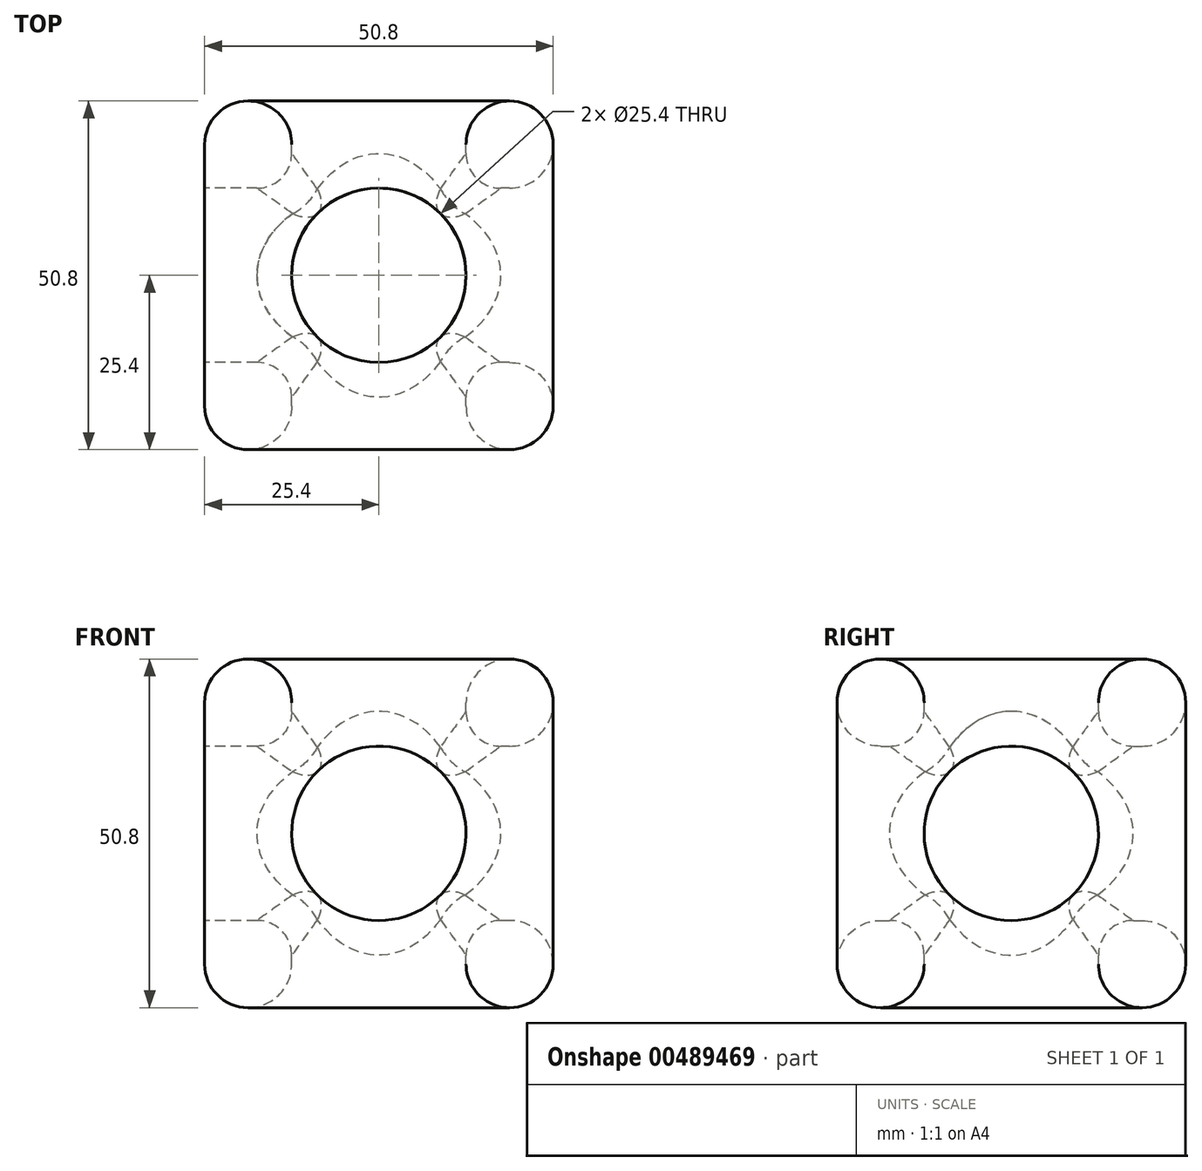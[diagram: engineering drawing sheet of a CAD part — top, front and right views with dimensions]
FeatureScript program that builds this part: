
annotation { "Feature Type Name" : "Feature", "Feature Type Description" : "" }
export const myFeature = defineFeature(function(context is Context, id is Id, definition is map)
    precondition{}
    {
        {
            var Q0;
            Q0=qCreatedBy(makeId("Front.planeOp"),FACE);
            var sketch = newSketch(context, id + "F0", { "sketchPlane" : qUnion([Q0])});
            skLineSegment(sketch, "E0", {"start": v(0, 0) * mm, "end": v(0, 50.8) * mm});
            skLineSegment(sketch, "E1", {"start": v(0, 50.8) * mm, "end": v(50.8, 50.8) * mm});
            skLineSegment(sketch, "E2", {"start": v(50.8, 50.8) * mm, "end": v(50.8, 0) * mm});
            skLineSegment(sketch, "E3", {"start": v(50.8, 0) * mm, "end": v(0, 0) * mm});
            skCircle(sketch, "E4", {"center": v(25.4, 25.4) * mm, "radius": 12.7 * mm});
            skSolve(sketch);
        }
        {
            var Q0;
            Q0 = qSketchRegion(id + "F0", true);
            extrude(context, id + "F1", {"entities" : qUnion([Q0]), "depth" : 50.8 * mm});
        }
        {
            var Q0;
            Q0=makeQuery(id+"F1.opExtrude","SWEPT_FACE",FACE,{"disambiguationData":[OSD([sQuery(id+"F0.wireOp",EDGE,"E0")])]});
            var sketch = newSketch(context, id + "F2", { "sketchPlane" : qUnion([Q0])});
            skPoint(sketch, "E5.trimOffspring.end.orphan", {"position": v(50.8, 50.8) * mm});
            skPoint(sketch, "E6.start.orphan", {"position": v(0, 50.8) * mm});
            skLineSegment(sketch, "E7", {"start": v(50.8, 0) * mm, "end": v(0, 0) * mm});
            skPoint(sketch, "E8.center.orphan", {"position": v(25.4, 50.8) * mm});
            skCircle(sketch, "E9", {"center": v(25.4, 25.4) * mm, "radius": 12.7 * mm});
            skSolve(sketch);
        }
        {
            var Q0;
            Q0 = qSketchRegion(id + "F2", true);
            extrude(context, id + "F3", {"entities" : qUnion([Q0]), "operationType" : NewBodyOperationType.REMOVE, "oppositeDirection" : true, "depth" : 50.8 * mm});
        }
        {
            var Q0;
            Q0 = qSketchRegion(id + "F2", true);
            extrude(context, id + "F4", {"entities" : qUnion([Q0]), "operationType" : NewBodyOperationType.REMOVE, "oppositeDirection" : true, "depth" : 50.8 * mm});
        }
        {
            var Q0;
            Q0=makeQuery(id+"F1.opExtrude","SWEPT_FACE",FACE,{"disambiguationData":[OSD([sQuery(id+"F0.wireOp",EDGE,"E1")])]});
            var sketch = newSketch(context, id + "F5", { "sketchPlane" : qUnion([Q0])});
            skCircle(sketch, "E10", {"center": v(25.4, -25.4) * mm, "radius": 12.7 * mm});
            skPoint(sketch, "E11.orphan", {"position": v(25.4, 0) * mm});
            skPoint(sketch, "E12.end.orphan", {"position": v(25.4, -50.8) * mm});
            skSolve(sketch);
        }
        {
            var Q0;
            Q0 = qSketchRegion(id + "F5", true);
            extrude(context, id + "F6", {"entities" : qUnion([Q0]), "operationType" : NewBodyOperationType.REMOVE, "oppositeDirection" : true, "depth" : 50.8 * mm});
        }
        {
            var Q0;
            Q0=makeQuery(id+"F1.opExtrude","SWEPT_EDGE",EDGE,{"disambiguationData":[OSD([sQuery(id+"F0.wireOp",EDGE,"E0"),sQuery(id+"F0.wireOp",EDGE,"E3")])]});
            var Q1;
            Q1=makeQuery(id+"F1.opExtrude","CAP_EDGE",EDGE,{"disambiguationData":[OSD([sQuery(id+"F0.wireOp",EDGE,"E0")])],"isStart":true});
            var Q2;
            Q2=makeQuery(id+"F1.opExtrude","SWEPT_FACE",FACE,{"disambiguationData":[OSD([sQuery(id+"F0.wireOp",EDGE,"E2")])]});
            var Q3;
            Q3=makeQuery(id+"F1.opExtrude","SWEPT_EDGE",EDGE,{"disambiguationData":[OSD([sQuery(id+"F0.wireOp",EDGE,"E2"),sQuery(id+"F0.wireOp",EDGE,"E3")])]});
            var Q4;
            Q4=makeQuery(id+"F1.opExtrude","CAP_EDGE",EDGE,{"disambiguationData":[OSD([sQuery(id+"F0.wireOp",EDGE,"E3")])],"isStart":true});
            var Q5;
            Q5=makeQuery(id+"F1.opExtrude","CAP_EDGE",EDGE,{"disambiguationData":[OSD([sQuery(id+"F0.wireOp",EDGE,"E3")])],"isStart":false});
            var Q6;
            Q6=makeQuery(id+"F6.boolean.opBoolean","COPY",EDGE,{"derivedFrom":makeQuery(id+"F6.opExtrude","CAP_EDGE",EDGE,{"disambiguationData":[OSD([sQuery(id+"F5.wireOp",EDGE,"E10")])],"isStart":false})});
            var Q7;
            Q7=makeQuery(id+"F1.opExtrude","SWEPT_FACE",FACE,{"disambiguationData":[OSD([sQuery(id+"F0.wireOp",EDGE,"E3")])]});
            var Q8;
            Q8=makeQuery(id+"F1.opExtrude","SWEPT_FACE",FACE,{"disambiguationData":[OSD([sQuery(id+"F0.wireOp",EDGE,"E1")])]});
            var Q9;
            Q9=makeQuery(id+"F3.boolean.opBoolean","COPY",EDGE,{"derivedFrom":makeQuery(id+"F3.opExtrude","CAP_EDGE",EDGE,{"disambiguationData":[OSD([sQuery(id+"F2.wireOp",EDGE,"E9")])],"isStart":true})});
            var Q10;
            Q10=makeQuery(id+"F1.opExtrude","CAP_EDGE",EDGE,{"disambiguationData":[OSD([sQuery(id+"F0.wireOp",EDGE,"E0")])],"isStart":false});
            var Q11;
            Q11=makeQuery(id+"F1.opExtrude","CAP_EDGE",EDGE,{"disambiguationData":[OSD([sQuery(id+"F0.wireOp",EDGE,"E4")])],"isStart":true});
            var Q12;
            Q12=makeQuery(id+"F1.opExtrude","CAP_EDGE",EDGE,{"disambiguationData":[OSD([sQuery(id+"F0.wireOp",EDGE,"E4")])],"isStart":false});
            fillet(context, id + "F7", {"entities" : qUnion([Q0, Q1, Q2, Q3, Q4, Q5, Q6, Q7, Q8, Q9, Q10, Q11, Q12]), "radius" : 6.35 * mm, "tangentPropagation" : true, "allowEdgeOverflow" : false});
        }
        {
            var Q0;
            {var subQ0=makeQuery(id+"F3.opExtrude","SWEPT_FACE",FACE,{"disambiguationData":[OSD([sQuery(id+"F2.wireOp",EDGE,"E9")])]});Q0=makeQuery(id+"F6.boolean.opBoolean","INTERSECT",EDGE,{"disambiguationData":[OD(1.0)],"derivedFrom":[makeQuery(id+"F3.boolean.opBoolean","COPY",FACE,{"disambiguationData":[TD([makeQuery(id+"F1.opExtrude","SWEPT_FACE",FACE,{"disambiguationData":[OSD([sQuery(id+"F0.wireOp",EDGE,"E2")])]})])],"derivedFrom":subQ0}),makeQuery(id+"F6.opExtrude","SWEPT_FACE",FACE,{"disambiguationData":[OSD([sQuery(id+"F5.wireOp",EDGE,"E10")])]})]});}
            var Q1;
            Q1=makeQuery(id+"F3.boolean.opBoolean","INTERSECT",EDGE,{"disambiguationData":[OD(3.0)],"derivedFrom":[makeQuery(id+"F1.opExtrude","SWEPT_FACE",FACE,{"disambiguationData":[OSD([sQuery(id+"F0.wireOp",EDGE,"E4")])]}),makeQuery(id+"F3.opExtrude","SWEPT_FACE",FACE,{"disambiguationData":[OSD([sQuery(id+"F2.wireOp",EDGE,"E9")])]})]});
            var Q2;
            {var subQ0=sQuery(id+"F0.wireOp",EDGE,"E4");var subQ1=makeQuery(id+"F1.opExtrude","SWEPT_FACE",FACE,{"disambiguationData":[OSD([subQ0])]});Q2=makeQuery(id+"F6.boolean.opBoolean","INTERSECT",EDGE,{"disambiguationData":[OD(1.0)],"derivedFrom":[makeQuery(id+"F3.boolean.opBoolean","SPLIT",FACE,{"disambiguationData":[TD([makeQuery(id+"F1.opExtrude","CAP_FACE",FACE,{"disambiguationData":[OSD([sQuery(id+"F0.wireOp",EDGE,"E0"),sQuery(id+"F0.wireOp",EDGE,"E1"),sQuery(id+"F0.wireOp",EDGE,"E2"),sQuery(id+"F0.wireOp",EDGE,"E3"),subQ0])],"isStart":false})])],"derivedFrom":subQ1}),makeQuery(id+"F6.opExtrude","SWEPT_FACE",FACE,{"disambiguationData":[OSD([sQuery(id+"F5.wireOp",EDGE,"E10")])]})]});}
            var Q3;
            {var subQ0=sQuery(id+"F0.wireOp",EDGE,"E4");var subQ1=makeQuery(id+"F1.opExtrude","SWEPT_FACE",FACE,{"disambiguationData":[OSD([subQ0])]});Q3=makeQuery(id+"F6.boolean.opBoolean","INTERSECT",EDGE,{"disambiguationData":[OD(0.0)],"derivedFrom":[makeQuery(id+"F3.boolean.opBoolean","SPLIT",FACE,{"disambiguationData":[TD([makeQuery(id+"F1.opExtrude","CAP_FACE",FACE,{"disambiguationData":[OSD([sQuery(id+"F0.wireOp",EDGE,"E0"),sQuery(id+"F0.wireOp",EDGE,"E1"),sQuery(id+"F0.wireOp",EDGE,"E2"),sQuery(id+"F0.wireOp",EDGE,"E3"),subQ0])],"isStart":false})])],"derivedFrom":subQ1}),makeQuery(id+"F6.opExtrude","SWEPT_FACE",FACE,{"disambiguationData":[OSD([sQuery(id+"F5.wireOp",EDGE,"E10")])]})]});}
            var Q4;
            Q4=makeQuery(id+"F3.boolean.opBoolean","INTERSECT",EDGE,{"disambiguationData":[OD(0.0)],"derivedFrom":[makeQuery(id+"F1.opExtrude","SWEPT_FACE",FACE,{"disambiguationData":[OSD([sQuery(id+"F0.wireOp",EDGE,"E4")])]}),makeQuery(id+"F3.opExtrude","SWEPT_FACE",FACE,{"disambiguationData":[OSD([sQuery(id+"F2.wireOp",EDGE,"E9")])]})]});
            var Q5;
            {var subQ0=makeQuery(id+"F3.opExtrude","SWEPT_FACE",FACE,{"disambiguationData":[OSD([sQuery(id+"F2.wireOp",EDGE,"E9")])]});Q5=makeQuery(id+"F6.boolean.opBoolean","INTERSECT",EDGE,{"disambiguationData":[OD(0.0)],"derivedFrom":[makeQuery(id+"F3.boolean.opBoolean","COPY",FACE,{"disambiguationData":[TD([makeQuery(id+"F1.opExtrude","SWEPT_FACE",FACE,{"disambiguationData":[OSD([sQuery(id+"F0.wireOp",EDGE,"E0")])]})])],"derivedFrom":subQ0}),makeQuery(id+"F6.opExtrude","SWEPT_FACE",FACE,{"disambiguationData":[OSD([sQuery(id+"F5.wireOp",EDGE,"E10")])]})]});}
            var Q6;
            Q6=makeQuery(id+"F3.boolean.opBoolean","INTERSECT",EDGE,{"disambiguationData":[OD(2.0)],"derivedFrom":[makeQuery(id+"F1.opExtrude","SWEPT_FACE",FACE,{"disambiguationData":[OSD([sQuery(id+"F0.wireOp",EDGE,"E4")])]}),makeQuery(id+"F3.opExtrude","SWEPT_FACE",FACE,{"disambiguationData":[OSD([sQuery(id+"F2.wireOp",EDGE,"E9")])]})]});
            var Q7;
            Q7=makeQuery(id+"F3.boolean.opBoolean","INTERSECT",EDGE,{"disambiguationData":[OD(1.0)],"derivedFrom":[makeQuery(id+"F1.opExtrude","SWEPT_FACE",FACE,{"disambiguationData":[OSD([sQuery(id+"F0.wireOp",EDGE,"E4")])]}),makeQuery(id+"F3.opExtrude","SWEPT_FACE",FACE,{"disambiguationData":[OSD([sQuery(id+"F2.wireOp",EDGE,"E9")])]})]});
            var Q8;
            {var subQ0=makeQuery(id+"F3.opExtrude","SWEPT_FACE",FACE,{"disambiguationData":[OSD([sQuery(id+"F2.wireOp",EDGE,"E9")])]});Q8=makeQuery(id+"F6.boolean.opBoolean","INTERSECT",EDGE,{"disambiguationData":[OD(0.0)],"derivedFrom":[makeQuery(id+"F3.boolean.opBoolean","COPY",FACE,{"disambiguationData":[TD([makeQuery(id+"F1.opExtrude","SWEPT_FACE",FACE,{"disambiguationData":[OSD([sQuery(id+"F0.wireOp",EDGE,"E2")])]})])],"derivedFrom":subQ0}),makeQuery(id+"F6.opExtrude","SWEPT_FACE",FACE,{"disambiguationData":[OSD([sQuery(id+"F5.wireOp",EDGE,"E10")])]})]});}
            var Q9;
            {var subQ0=sQuery(id+"F0.wireOp",EDGE,"E4");var subQ1=makeQuery(id+"F1.opExtrude","SWEPT_FACE",FACE,{"disambiguationData":[OSD([subQ0])]});Q9=makeQuery(id+"F6.boolean.opBoolean","INTERSECT",EDGE,{"disambiguationData":[OD(0.0)],"derivedFrom":[makeQuery(id+"F3.boolean.opBoolean","SPLIT",FACE,{"disambiguationData":[TD([makeQuery(id+"F1.opExtrude","CAP_FACE",FACE,{"disambiguationData":[OSD([sQuery(id+"F0.wireOp",EDGE,"E0"),sQuery(id+"F0.wireOp",EDGE,"E1"),sQuery(id+"F0.wireOp",EDGE,"E2"),sQuery(id+"F0.wireOp",EDGE,"E3"),subQ0])],"isStart":true})])],"derivedFrom":subQ1}),makeQuery(id+"F6.opExtrude","SWEPT_FACE",FACE,{"disambiguationData":[OSD([sQuery(id+"F5.wireOp",EDGE,"E10")])]})]});}
            var Q10;
            {var subQ0=sQuery(id+"F0.wireOp",EDGE,"E4");var subQ1=makeQuery(id+"F1.opExtrude","SWEPT_FACE",FACE,{"disambiguationData":[OSD([subQ0])]});Q10=makeQuery(id+"F6.boolean.opBoolean","INTERSECT",EDGE,{"disambiguationData":[OD(1.0)],"derivedFrom":[makeQuery(id+"F3.boolean.opBoolean","SPLIT",FACE,{"disambiguationData":[TD([makeQuery(id+"F1.opExtrude","CAP_FACE",FACE,{"disambiguationData":[OSD([sQuery(id+"F0.wireOp",EDGE,"E0"),sQuery(id+"F0.wireOp",EDGE,"E1"),sQuery(id+"F0.wireOp",EDGE,"E2"),sQuery(id+"F0.wireOp",EDGE,"E3"),subQ0])],"isStart":true})])],"derivedFrom":subQ1}),makeQuery(id+"F6.opExtrude","SWEPT_FACE",FACE,{"disambiguationData":[OSD([sQuery(id+"F5.wireOp",EDGE,"E10")])]})]});}
            var Q11;
            {var subQ0=makeQuery(id+"F3.opExtrude","SWEPT_FACE",FACE,{"disambiguationData":[OSD([sQuery(id+"F2.wireOp",EDGE,"E9")])]});Q11=makeQuery(id+"F6.boolean.opBoolean","INTERSECT",EDGE,{"disambiguationData":[OD(1.0)],"derivedFrom":[makeQuery(id+"F3.boolean.opBoolean","COPY",FACE,{"disambiguationData":[TD([makeQuery(id+"F1.opExtrude","SWEPT_FACE",FACE,{"disambiguationData":[OSD([sQuery(id+"F0.wireOp",EDGE,"E0")])]})])],"derivedFrom":subQ0}),makeQuery(id+"F6.opExtrude","SWEPT_FACE",FACE,{"disambiguationData":[OSD([sQuery(id+"F5.wireOp",EDGE,"E10")])]})]});}
            fillet(context, id + "F8", {"entities" : qUnion([Q0, Q1, Q2, Q3, Q4, Q5, Q6, Q7, Q8, Q9, Q10, Q11]), "radius" : 5.08 * mm, "tangentPropagation" : true, "allowEdgeOverflow" : false});
        }
    });
